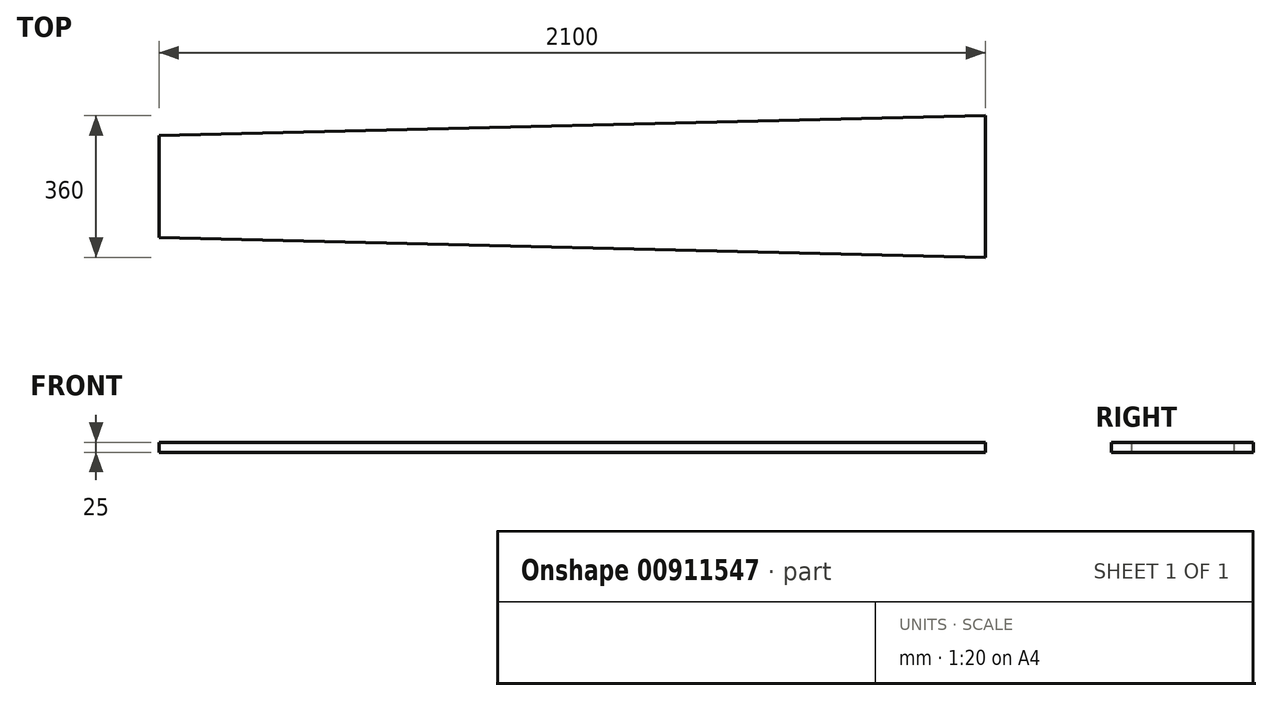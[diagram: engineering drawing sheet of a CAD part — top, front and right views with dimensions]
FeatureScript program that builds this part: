
annotation { "Feature Type Name" : "Feature", "Feature Type Description" : "" }
export const myFeature = defineFeature(function(context is Context, id is Id, definition is map)
    precondition{}
    {
        {
            var Q0;
            Q0=qCreatedBy(makeId("Top.planeOp"),FACE);
            var sketch = newSketch(context, id + "F0", { "sketchPlane" : qUnion([Q0])});
            skLineSegment(sketch, "E0", {"start": v(0, 0) * mm, "end": v(0, -360) * mm});
            skLineSegment(sketch, "E1", {"start": v(0, -360) * mm, "end": v(-2100, -310) * mm});
            skLineSegment(sketch, "E2", {"start": v(-2100, -310) * mm, "end": v(-2100, -50) * mm});
            skLineSegment(sketch, "E3", {"start": v(-2100, -50) * mm, "end": v(0, 0) * mm});
            skSolve(sketch);
        }
        {
            var Q0;
            Q0=makeQuery(id+"F0.imprint","IMPRINT",FACE,{"disambiguationData":[TD([[makeQuery(id+"F0.imprint","IMPRINT",EDGE,{"derivedFrom":sQuery(id+"F0.wireOp",EDGE,"E0")}),-1.0]])]});
            extrude(context, id + "F1", {"entities" : qUnion([Q0]), "depth" : 25 * mm, "offsetDistance" : 25 * mm});
        }
        {
            var Q0;
            Q0=makeQuery(id+"F1.opExtrude","CAP_FACE",FACE,{"disambiguationData":[OSD([sQuery(id+"F0.wireOp",EDGE,"E0"),sQuery(id+"F0.wireOp",EDGE,"E1"),sQuery(id+"F0.wireOp",EDGE,"E2"),sQuery(id+"F0.wireOp",EDGE,"E3")])],"isStart":false});
            var sketch = newSketch(context, id + "F2", { "sketchPlane" : qUnion([Q0])});
            skLineSegment(sketch, "E4", {"start": v(0, -360) * mm, "end": v(32.84, -908.53) * mm});
            skLineSegment(sketch, "E5", {"start": v(32.84, -908.53) * mm, "end": v(103.84, -1328.61) * mm});
            skLineSegment(sketch, "E6", {"start": v(103.84, -1328.61) * mm, "end": v(234.01, -1328.61) * mm});
            skLineSegment(sketch, "E7", {"start": v(234.01, -1328.61) * mm, "end": v(193.98, 1467.54) * mm});
            skLineSegment(sketch, "E8", {"start": v(193.98, 1467.54) * mm, "end": v(68.26, 1411.17) * mm});
            skLineSegment(sketch, "E9", {"start": v(68.26, 1411.17) * mm, "end": v(-87.27, 1199.26) * mm});
            skLineSegment(sketch, "E10", {"start": v(-87.27, 1199.26) * mm, "end": v(-128.09, 896.15) * mm});
            skLineSegment(sketch, "E11", {"start": v(-128.09, 896.15) * mm, "end": v(-80.07, 367.2) * mm});
            skLineSegment(sketch, "E12", {"start": v(-80.07, 367.2) * mm, "end": v(0, 0) * mm});
            skSolve(sketch);
        }
        {
            var Q0;
            Q0=makeQuery(id+"F2.imprint","IMPRINT",FACE,{"disambiguationData":[TD([[makeQuery(id+"F2.imprint","IMPRINT",EDGE,{"derivedFrom":sQuery(id+"F2.wireOp",EDGE,"E4")}),1.0]])]});
            var Q1;
            Q1=sQuery(id+"F2.wireOp",EDGE,"E7");
            revolve(context, id + "F3", {"surfaceOperationType" : NewSurfaceOperationType.NEW, "entities" : qUnion([Q0]), "axis" : qUnion([Q1]), "revolveType" : RevolveType.FULL});
        }
        {
            var Q0;
            Q0=makeQuery(id+"F3.opRevolve","SWEPT_BODY",BODY,{"disambiguationData":[OSD([sQuery(id+"F0.wireOp",EDGE,"E0"),sQuery(id+"F2.wireOp",EDGE,"E4"),sQuery(id+"F2.wireOp",EDGE,"E5"),sQuery(id+"F2.wireOp",EDGE,"E6"),sQuery(id+"F2.wireOp",EDGE,"E7"),sQuery(id+"F2.wireOp",EDGE,"E8"),sQuery(id+"F2.wireOp",EDGE,"E9"),sQuery(id+"F2.wireOp",EDGE,"E10"),sQuery(id+"F2.wireOp",EDGE,"E11"),sQuery(id+"F2.wireOp",EDGE,"E12")])]});
            deleteBodies(context, id + "F4", {"entities" : qUnion([Q0])});
        }
    });
